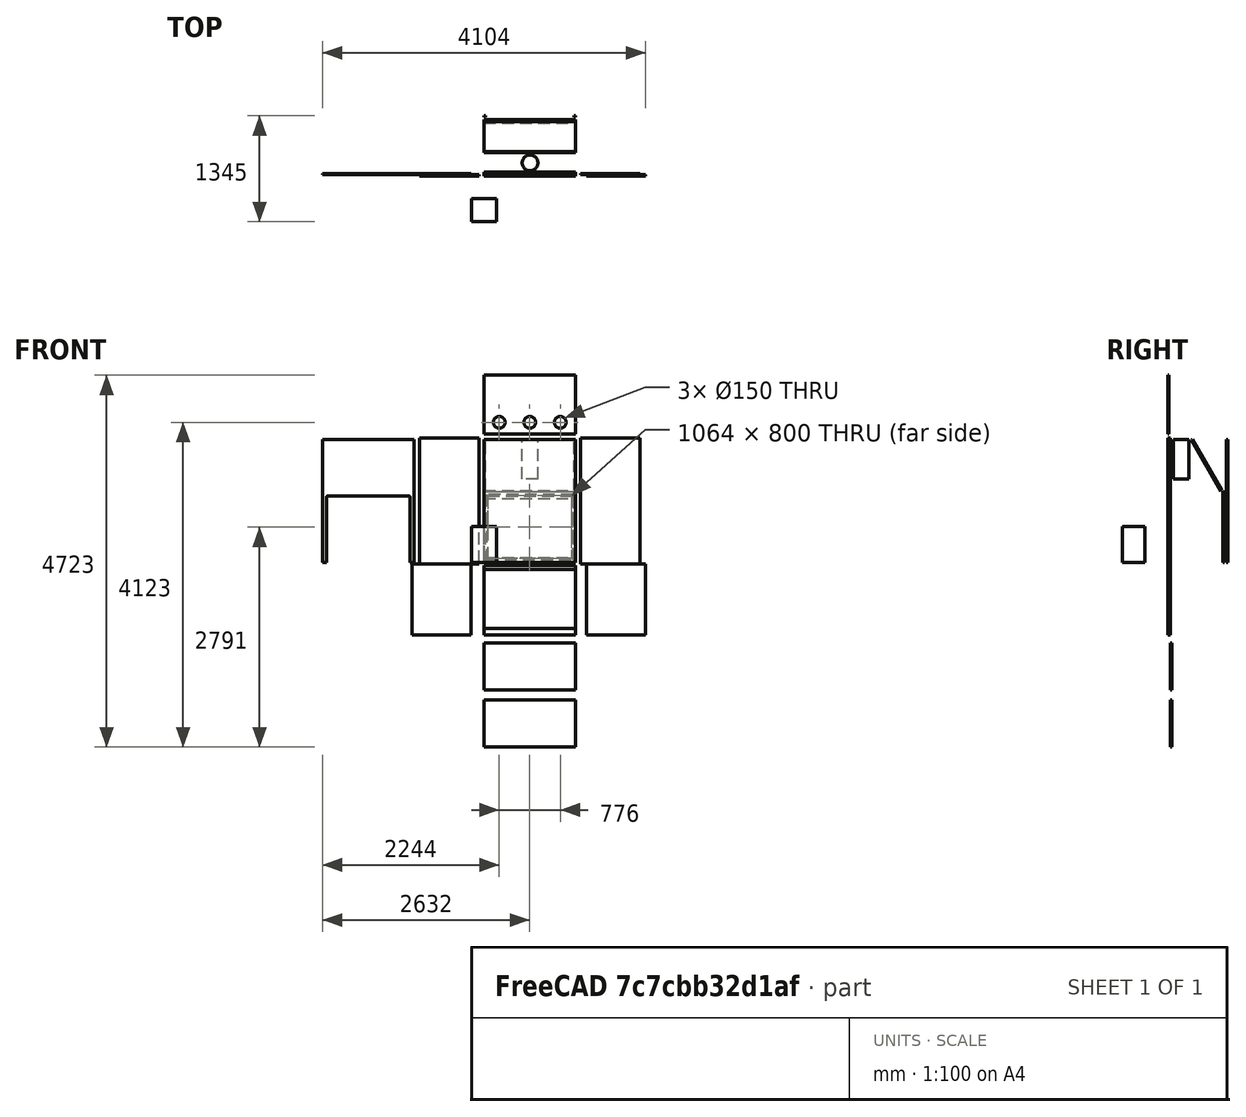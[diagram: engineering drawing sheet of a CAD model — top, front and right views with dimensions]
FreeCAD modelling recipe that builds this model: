
FCSTD DOCUMENT  (FreeCAD 0.18R4 (GitTag))
Label: fumehood1200_flat
License: All rights reserved
LicenseURL: http://en.wikipedia.org/wiki/All_rights_reserved
objects: TechDraw::DrawViewDimension×32, TechDraw::DrawProjGroup×14, Part::Box×13, TechDraw::DrawProjGroupItem×13, Sketcher::SketchObject×7, PartDesign::Body×5, PartDesign::Pad×4, App::Part×4, TechDraw::DrawSVGTemplate×3, TechDraw::DrawPage×3, PartDesign::Pocket×2, Spreadsheet::Sheet×1, Part::Cylinder×1
note: 38 computed .brp shape members not serialized (recipe doc carries the construction recipe); baked Part::Feature solids carry a one-line shape summary decoded from their .brp

FEATURE [Spreadsheet::Sheet] Spreadsheet  label="dim"
  cells = B2=Width; C2(dim_width)=1200; E2=FrontEdge; F2(dim_frontedge)=50; B3=Height; C3(dim_height)=1600; E3=FrontRadius; F3(dim_frontradius)=25; B4=Depth; C4(dim_depth)=750; E4=FrontOpening; F4(dim_frontopening)=850; B5=Thickness; C5(dim_thickness)=18; B6=Elevation; C6(dim_elevation)=900; B8=WindowWidth; C8(dim_windowwidth)==dim_width - dim_thickness * 2; B9=WindowHeight; C9(dim_windowheight)=900; B10=WindowEdge; C10(dim_windowedge)=50
FEATURE [Part::Box] Box  label="BackWall"
  AttacherType = Attacher::AttachEngine3D
  Height = 1564
  Length = 1164
  Placement = pos=(0,-18,18) rot=(0,0,1;0rad)
  Width = 18
  expr: Width = dim.dim_thickness
  expr: Height = dim.dim_height - 2 * dim.dim_thickness
  expr: Length = dim.dim_width - 2 * dim.dim_thickness
FEATURE [Part::Box] Box001  label="Side1"
  AttacherType = Attacher::AttachEngine3D
  Height = 1600
  Length = 750
  Placement = pos=(1230,0,0) rot=(0,0,1;0rad)
  Width = 18
  expr: Height = dim.dim_height
  expr: Width = dim.dim_thickness
  expr: Length = dim.dim_depth
FEATURE [Part::Box] Box002  label="Side2"
  AttacherType = Attacher::AttachEngine3D
  Height = 1600
  Length = 750
  Placement = pos=(-65,1.44e-14,0) rot=(0,0,1;3.14159rad)
  Width = 18
  expr: Height = dim.dim_height
  expr: Width = dim.dim_thickness
  expr: Length = dim.dim_depth
FEATURE [Part::Box] Box004  label="Bottom"
  AttacherType = Attacher::AttachEngine3D
  Height = 750
  Length = 1164
  Placement = pos=(0,4e-15,-70) rot=(1,0,0;3.14159rad)
  Width = 18
  expr: Height = dim.dim_depth
  expr: Width = dim.dim_thickness
  expr: Length = dim.dim_width - 2 * dim.dim_thickness
FEATURE [Sketcher::SketchObject] Sketch
  MapMode = 5
  Placement = pos=(0,0,0) rot=(1,0,0;1.5708rad)
  Support = -> [XZ_Plane]
  expr: Constraints[26] = dim.dim_frontedge
  expr: Constraints[16] = dim.dim_frontopening
  expr: Constraints[14] = dim.dim_frontradius
  expr: Constraints[6] = dim.dim_height - 2 * dim.dim_thickness
  expr: Constraints[5] = dim.dim_width - 2 * dim.dim_thickness
  sketch-geometry (10):
    g0: LineSegment StartX=1164 StartY=0 StartZ=0 EndX=1164 EndY=1564 EndZ=0
    g1: LineSegment StartX=1164 StartY=1564 StartZ=0 EndX=0 EndY=1564 EndZ=0
    g2: LineSegment StartX=0 StartY=1564 StartZ=0 EndX=0 EndY=0 EndZ=0
    g3: LineSegment StartX=75 StartY=850 StartZ=0 EndX=1089 EndY=850 EndZ=0
    g4: LineSegment StartX=1114 StartY=825 StartZ=0 EndX=1114 EndY=0 EndZ=0
    g5: LineSegment StartX=50 StartY=0 StartZ=0 EndX=50 EndY=825 EndZ=0
    g6: ArcOfCircle CenterX=75 CenterY=825 CenterZ=0 NormalX=0 NormalY=0 NormalZ=1 AngleXU=0 Radius=25 StartAngle=1.5708 EndAngle=3.14159
    g7: ArcOfCircle CenterX=1089 CenterY=825 CenterZ=0 NormalX=0 NormalY=0 NormalZ=1 AngleXU=0 Radius=25 StartAngle=-1.8e-15 EndAngle=1.5708
    g8: LineSegment StartX=1114 StartY=0 StartZ=0 EndX=1164 EndY=0 EndZ=0
    g9: LineSegment StartX=0 StartY=0 StartZ=0 EndX=50 EndY=0 EndZ=0
  constraints (27):
    c: Coincident(g0,g1)
    c: Coincident(g1,g2)
    c: Horizontal(g1)
    c: Vertical(g0)
    c: Vertical(g2)
    c: DistanceX(g1,g1) = 1164
    c: DistanceY(g0,g0) = 1564
    c: Horizontal(g3)
    c: Vertical(g4)
    c: Vertical(g5)
    c: Tangent(g5,g6) = 1.5708
    c: Tangent(g3,g6) = 1.5708
    c: Tangent(g3,g7) = 1.5708
    c: Tangent(g4,g7) = 1.5708
    c: Radius(g6) = 25
    c: Equal(g6,g7)
    c: DistanceY(g2,g3) = 850
    c: PointOnObject(g5,g-1)
    c: PointOnObject(g4,g-1)
    c: PointOnObject(g0,g-1)
    c: Coincident(g8,g4)
    c: Coincident(g8,g0)
    c: Coincident(g2,g-1)
    c: Coincident(g9,g2)
    c: Coincident(g9,g5)
    c: Equal(g9,g8)
    c: DistanceX(g9,g9) = 50
FEATURE [PartDesign::Pad] Pad
  Length = 18
  Length2 = 100
  Placement = pos=(0,0,0) rot=(1,0,0;1.5708rad)
  Profile = -> Sketch
  Reversed = true
  Type = 0
  expr: Length = dim.dim_thickness
FEATURE [PartDesign::Body] Body  label="Front"
  Group = -> [Sketch,Pad]
  Origin = -> Origin
  Placement = pos=(-2050,0,18) rot=(0,0,1;0rad)
  Tip = -> Pad
FEATURE [Sketcher::SketchObject] Sketch001
  MapMode = 5
  Placement = pos=(0,0,0) rot=(1,0,0;1.5708rad)
  Support = -> [XZ_Plane001]
  expr: Constraints[34] = dim.dim_windowedge
  expr: Constraints[18] = dim.dim_windowheight
  expr: Constraints[17] = dim.dim_windowwidth
  sketch-geometry (12):
    g0: LineSegment StartX=0 StartY=0 StartZ=0 EndX=-1064 EndY=0 EndZ=0
    g1: LineSegment StartX=-1064 StartY=0 StartZ=0 EndX=-1064 EndY=800 EndZ=0
    g2: LineSegment StartX=-1064 StartY=800 StartZ=0 EndX=0 EndY=800 EndZ=0
    g3: LineSegment StartX=0 StartY=800 StartZ=0 EndX=0 EndY=0 EndZ=0
    g4: LineSegment StartX=50 StartY=850 StartZ=0 EndX=-1114 EndY=850 EndZ=0
    g5: LineSegment StartX=-1114 StartY=850 StartZ=0 EndX=-1114 EndY=-50 EndZ=0
    g6: LineSegment StartX=-1114 StartY=-50 StartZ=0 EndX=50 EndY=-50 EndZ=0
    g7: LineSegment StartX=50 StartY=-50 StartZ=0 EndX=50 EndY=850 EndZ=0
    g8: LineSegment [constr] StartX=-1064 StartY=800 StartZ=0 EndX=-1114 EndY=800 EndZ=0
    g9: LineSegment [constr] StartX=-1064 StartY=800 StartZ=0 EndX=-1064 EndY=850 EndZ=0
    g10: LineSegment [constr] StartX=0 StartY=0 StartZ=0 EndX=50 EndY=0 EndZ=0
    g11: LineSegment [constr] StartX=0 StartY=0 StartZ=0 EndX=0 EndY=-50 EndZ=0
  constraints (35):
    c: Coincident(g0,g1)
    c: Coincident(g1,g2)
    c: Coincident(g2,g3)
    c: Coincident(g3,g0)
    c: Horizontal(g0)
    c: Horizontal(g2)
    c: Vertical(g1)
    c: Vertical(g3)
    c: Coincident(g0,g-1)
    c: Coincident(g4,g5)
    c: Coincident(g5,g6)
    c: Coincident(g6,g7)
    c: Coincident(g7,g4)
    c: Horizontal(g4)
    c: Horizontal(g6)
    c: Vertical(g5)
    c: Vertical(g7)
    c: DistanceX(g4,g4) = 1164
    c: DistanceY(g5,g5) = 900
    c: Coincident(g8,g1)
    c: PointOnObject(g8,g5)
    c: Horizontal(g8)
    c: Coincident(g9,g1)
    c: PointOnObject(g9,g4)
    c: Vertical(g9)
    c: Coincident(g10,g0)
    c: PointOnObject(g10,g7)
    c: Coincident(g11,g0)
    c: PointOnObject(g11,g6)
    c: Horizontal(g10)
    c: Vertical(g11)
    c: Equal(g10,g11)
    c: Equal(g11,g8)
    c: Equal(g8,g9)
    c: DistanceX(g8,g8) = 50
FEATURE [PartDesign::Pad] Pad001
  Length = 18
  Length2 = 100
  Placement = pos=(0,0,0) rot=(1,0,0;1.5708rad)
  Profile = -> Sketch001
  Type = 0
  expr: Length = dim.dim_thickness
FEATURE [Sketcher::SketchObject] Sketch010
  MapMode = 5
  Support = -> [XY_Plane010]
  sketch-geometry (7):
    g0: LineSegment StartX=-160 StartY=145 StartZ=0 EndX=160 EndY=145 EndZ=0
    g1: LineSegment StartX=160 StartY=145 StartZ=0 EndX=160 EndY=-145 EndZ=0
    g2: LineSegment StartX=160 StartY=-145 StartZ=0 EndX=-160 EndY=-145 EndZ=0
    g3: LineSegment StartX=-160 StartY=-145 StartZ=0 EndX=-160 EndY=145 EndZ=0
    g4: LineSegment [constr] StartX=-160 StartY=145 StartZ=0 EndX=0 EndY=0 EndZ=0
    g5: LineSegment [constr] StartX=0 StartY=0 StartZ=0 EndX=160 EndY=145 EndZ=0
    g6: LineSegment [constr] StartX=160 StartY=-145 StartZ=0 EndX=0 EndY=0 EndZ=0
  constraints (18):
    c: Coincident(g0,g1)
    c: Coincident(g1,g2)
    c: Coincident(g2,g3)
    c: Coincident(g3,g0)
    c: Horizontal(g0)
    c: Horizontal(g2)
    c: Vertical(g1)
    c: Vertical(g3)
    c: DistanceY(g3,g3) = 290
    c: DistanceX(g0,g0) = 320
    c: Coincident(g0,g4)
    c: Coincident(g4,g-1)
    c: Coincident(g4,g5)
    c: Coincident(g5,g0)
    c: Coincident(g1,g6)
    c: Coincident(g6,g-1)
    c: Equal(g6,g5)
    c: Equal(g5,g4)
FEATURE [PartDesign::Pad] Pad010
  Length = 460
  Length2 = 100
  Profile = -> Sketch010
  Type = 0
FEATURE [PartDesign::Body] Body008  label="Printer"
  Group = -> [Sketch010,Pad010]
  Origin = -> Origin010
  Placement = pos=(0,-450,20) rot=(0,0,1;0rad)
  Tip = -> Pad010
FEATURE [Sketcher::SketchObject] Sketch011
  MapMode = 5
  Placement = pos=(0,0,0) rot=(0.57735,0.57735,0.57735;2.0944rad)
  Support = -> [YZ_Plane011]
  sketch-geometry (17):
    g0: LineSegment StartX=337.533 StartY=73.563 StartZ=0 EndX=380.615 EndY=-384.066 EndZ=0
    g1: LineSegment StartX=380.615 StartY=-384.066 StartZ=0 EndX=395.57 EndY=-900 EndZ=0
    g2: LineSegment StartX=395.57 StartY=-900 StartZ=0 EndX=136.956 EndY=-900 EndZ=0
    g3: LineSegment StartX=337.533 StartY=73.563 StartZ=0 EndX=268.981 EndY=671.761 EndZ=0
    g4: LineSegment StartX=268.981 StartY=671.761 StartZ=0 EndX=434.918 EndY=671.761 EndZ=0
    g5: LineSegment StartX=434.918 StartY=671.761 StartZ=0 EndX=337.533 EndY=73.563 EndZ=0
    g6: Circle CenterX=341.02 CenterY=900 CenterZ=0 NormalX=0 NormalY=0 NormalZ=1 AngleXU=0 Radius=148.256
    g7: LineSegment StartX=268.981 StartY=671.761 StartZ=0 EndX=257.081 EndY=260 EndZ=0
    g8: LineSegment StartX=257.081 StartY=260 StartZ=0 EndX=434.918 EndY=671.761 EndZ=0
    g9: LineSegment StartX=257.081 StartY=260 StartZ=0 EndX=-129.183 EndY=320.639 EndZ=0
    g10: LineSegment StartX=-129.183 StartY=320.639 StartZ=0 EndX=-129.183 EndY=239.552 EndZ=0
    g11: LineSegment StartX=-129.183 StartY=239.552 StartZ=0 EndX=257.081 EndY=260 EndZ=0
    g12: LineSegment StartX=337.533 StartY=73.563 StartZ=0 EndX=292.125 EndY=-384.066 EndZ=0
    g13: LineSegment StartX=292.125 StartY=-384.066 StartZ=0 EndX=395.57 EndY=-900 EndZ=0
    g14: LineSegment StartX=292.125 StartY=-384.066 StartZ=0 EndX=380.615 EndY=-384.066 EndZ=0
    g15: LineSegment StartX=-129.183 StartY=320.639 StartZ=0 EndX=-200.089 EndY=304.859 EndZ=0
    g16: LineSegment StartX=-129.183 StartY=239.552 StartZ=0 EndX=-200.089 EndY=304.859 EndZ=0
  constraints (28):
    c: Coincident(g1,g0)
    c: Coincident(g2,g1)
    c: Horizontal(g2)
    c: DistanceY(g2,g-1) = 900
    c: Coincident(g3,g0)
    c: Coincident(g4,g3)
    c: Horizontal(g4)
    c: Coincident(g5,g4)
    c: Coincident(g5,g0)
    c: DistanceY(g2,g6) = 1800
    c: Coincident(g7,g3)
    c: Coincident(g8,g7)
    c: Coincident(g8,g4)
    c: Coincident(g7,g9)
    c: Coincident(g9,g10)
    c: Vertical(g10)
    c: Coincident(g10,g11)
    c: Coincident(g11,g9)
    c: Coincident(g0,g12)
    c: Coincident(g12,g13)
    c: Coincident(g13,g1)
    c: Coincident(g14,g12)
    c: Coincident(g14,g0)
    c: Horizontal(g14)
    c: DistanceY(g1,g7) = 1160
    c: Coincident(g15,g9)
    c: Coincident(g16,g10)
    c: Coincident(g16,g15)
FEATURE [PartDesign::Body] Body009  label="human"
  Group = -> [Sketch011]
  Origin = -> Origin011
  Placement = pos=(0,-140,0) rot=(0,0,1;0rad)
FEATURE [App::Part] Part  label="Human"
  Group = -> [Body008,Body009]
  Origin = -> Origin002
  Placement = pos=(400,800,0) rot=(0,0,1;0rad)
FEATURE [Part::Box] Box005  label="Rail1"
  AttacherType = Attacher::AttachEngine3D
  Height = 1564
  Length = 20
  Placement = pos=(1144,730,18) rot=(0,0,1;0rad)
  Width = 20
  expr: Height = dim.dim_height - dim.dim_thickness * 2
FEATURE [Part::Box] Box006  label="Rail2"
  AttacherType = Attacher::AttachEngine3D
  Height = 1564
  Length = 20
  Placement = pos=(0,730,18) rot=(0,0,1;0rad)
  Width = 20
  expr: Height = dim.dim_height - dim.dim_thickness * 2
FEATURE [Sketcher::SketchObject] Sketch012
  ExternalGeometry = -> [Pad001]
  MapMode = 5
  Placement = pos=(0,0,0) rot=(-1,0,0;1.5708rad)
  Support = -> [Pad001]
  sketch-geometry (8):
    g0: LineSegment StartX=-1079 StartY=15 StartZ=0 EndX=15 EndY=15 EndZ=0
    g1: LineSegment StartX=15 StartY=15 StartZ=0 EndX=15 EndY=-815 EndZ=0
    g2: LineSegment StartX=15 StartY=-815 StartZ=0 EndX=-1079 EndY=-815 EndZ=0
    g3: LineSegment StartX=-1079 StartY=-815 StartZ=0 EndX=-1079 EndY=15 EndZ=0
    g4: LineSegment [constr] StartX=-1064 StartY=0 StartZ=0 EndX=-1079 EndY=0 EndZ=0
    g5: LineSegment [constr] StartX=-1064 StartY=0 StartZ=0 EndX=-1064 EndY=15 EndZ=0
    g6: LineSegment [constr] StartX=0 StartY=-800 StartZ=0 EndX=15 EndY=-800 EndZ=0
    g7: LineSegment [constr] StartX=0 StartY=-800 StartZ=0 EndX=0 EndY=-815 EndZ=0
  constraints (24):
    c: Coincident(g0,g1)
    c: Coincident(g1,g2)
    c: Coincident(g2,g3)
    c: Coincident(g3,g0)
    c: Horizontal(g0)
    c: Horizontal(g2)
    c: Vertical(g1)
    c: Vertical(g3)
    c: Coincident(g4,g-3)
    c: PointOnObject(g4,g3)
    c: Horizontal(g4)
    c: Coincident(g5,g4)
    c: PointOnObject(g5,g0)
    c: Vertical(g5)
    c: Coincident(g6,g-4)
    c: PointOnObject(g6,g1)
    c: Horizontal(g6)
    c: Coincident(g7,g6)
    c: PointOnObject(g7,g2)
    c: Vertical(g7)
    c: Equal(g6,g7)
    c: Equal(g7,g4)
    c: Equal(g4,g5)
    c: DistanceX(g4,g4) = 15
FEATURE [PartDesign::Pocket] Pocket
  BaseFeature = -> Pad001
  Length = 6
  Length2 = 100
  Placement = pos=(0,0,0) rot=(1,0,0;1.5708rad)
  Profile = -> Sketch012
  Type = 0
FEATURE [PartDesign::Body] Body001  label="Window"
  Group = -> [Sketch001,Pad001,Sketch012,Pocket]
  Origin = -> Origin001
  Placement = pos=(1114,700,68) rot=(0,0,1;0rad)
  Tip = -> Pocket
  expr: Placement.Base.x = dim.dim_width - 2 * dim.dim_thickness - 50
FEATURE [App::Part] Part001  label="Window001"
  Group = -> [Body001]
  Origin = -> Origin012
  Placement = pos=(0,0,350) rot=(0,0,1;0rad)
FEATURE [Part::Box] Box007  label="ShelfSide1"
  AttacherType = Attacher::AttachEngine3D
  Height = 900
  Length = 18
  Placement = pos=(-166,-3.29e-14,-900) rot=(0,0,1;1.5708rad)
  Width = 750
  expr: Length = dim.dim_thickness
  expr: Width = dim.dim_depth
  expr: Height = dim.dim_elevation
FEATURE [Part::Box] Box008  label="ShelfSide2"
  AttacherType = Attacher::AttachEngine3D
  Height = 900
  Length = 18
  Placement = pos=(1304,-3.11e-14,-900) rot=(0,0,1;4.71239rad)
  Width = 750
  expr: Height = dim.dim_elevation
  expr: Width = dim.dim_depth
  expr: Length = dim.dim_thickness
FEATURE [Part::Box] Box009  label="ShelfTop"
  AttacherType = Attacher::AttachEngine3D
  Height = 750
  Length = 1164
  Placement = pos=(0,-1.89e-14,85) rot=(0,0,1;0rad)
  Width = 18
  expr: Height = dim.dim_depth
  expr: Width = dim.dim_thickness
  expr: Length = dim.dim_width - 2 * dim.dim_thickness
FEATURE [Part::Box] Box010  label="ShelfBack"
  AttacherType = Attacher::AttachEngine3D
  Height = 882
  Length = 1164
  Placement = pos=(0,0,-900) rot=(0,0,1;0rad)
  Width = 18
  expr: Width = dim.dim_thickness
  expr: Height = dim.dim_elevation - dim.dim_thickness
  expr: Length = dim.dim_width - 2 * dim.dim_thickness
FEATURE [Part::Box] Box011  label="ShelfMid1"
  AttacherType = Attacher::AttachEngine3D
  Height = 18
  Length = 1164
  Placement = pos=(0,18,-1000) rot=(1,0,0;4.71239rad)
  Width = 600
  expr: Length = dim.dim_width - 2 * dim.dim_thickness
  expr: Width = dim.dim_depth - 150
  expr: Height = dim.dim_thickness
FEATURE [Part::Box] Box012  label="ShelfMid2"
  AttacherType = Attacher::AttachEngine3D
  Height = 18
  Length = 1164
  Placement = pos=(0,18,-1723) rot=(1,0,0;4.71239rad)
  Width = 600
  expr: Height = dim.dim_thickness
  expr: Width = dim.dim_depth - 150
  expr: Length = dim.dim_width - 2 * dim.dim_thickness
FEATURE [App::Part] Part002  label="Shelf"
  Group = -> [Box007,Box008,Box009,Box010,Box011,Box012]
  Origin = -> Origin013
  Placement = pos=(0,0,-1000) rot=(0,0,1;0rad)
FEATURE [Part::Cylinder] Cylinder
  Angle = 360
  AttacherType = Attacher::AttachEngine3D
  Height = 500
  Placement = pos=(586,152,1082) rot=(0,0,1;0rad)
  Radius = 100
FEATURE [Part::Box] Box013  label="Airway"
  AttacherType = Attacher::AttachEngine3D
  Height = 750
  Length = 1164
  Placement = pos=(0,298,1582) rot=(1,0,0;3.66519rad)
  Width = 18
  expr: Width = dim.dim_thickness
  expr: Length = dim.dim_width - 2 * dim.dim_thickness
FEATURE [Sketcher::SketchObject] Sketch013
  MapMode = 5
  Support = -> [XY_Plane014]
  expr: Constraints[10] = dim.dim_width - 2 * dim.dim_thickness
  expr: Constraints[9] = dim.dim_depth
  sketch-geometry (4):
    g0: LineSegment StartX=0 StartY=0 StartZ=0 EndX=1164 EndY=0 EndZ=0
    g1: LineSegment StartX=1164 StartY=0 StartZ=0 EndX=1164 EndY=750 EndZ=0
    g2: LineSegment StartX=1164 StartY=750 StartZ=0 EndX=0 EndY=750 EndZ=0
    g3: LineSegment StartX=0 StartY=750 StartZ=0 EndX=0 EndY=0 EndZ=0
  constraints (11):
    c: Coincident(g0,g1)
    c: Coincident(g1,g2)
    c: Coincident(g2,g3)
    c: Coincident(g3,g0)
    c: Horizontal(g0)
    c: Horizontal(g2)
    c: Vertical(g1)
    c: Vertical(g3)
    c: Coincident(g0,g-1)
    c: DistanceY(g1,g1) = 750
    c: DistanceX(g2,g2) = 1164
FEATURE [PartDesign::Pad] Pad011
  Length = 18
  Length2 = 100
  Profile = -> Sketch013
  Type = 0
  expr: Length = dim.dim_thickness
FEATURE [Sketcher::SketchObject] Sketch014
  ExternalGeometry = -> [Pad011]
  MapMode = 5
  Placement = pos=(0,0,18) rot=(0,0,1;0rad)
  Support = -> [Pad011]
  sketch-geometry (11):
    g0: LineSegment [constr] StartX=0 StartY=0 StartZ=0 EndX=194 EndY=150 EndZ=0
    g1: LineSegment [constr] StartX=194 StartY=150 StartZ=0 EndX=388 EndY=0 EndZ=0
    g2: LineSegment [constr] StartX=388 StartY=0 StartZ=0 EndX=582 EndY=150 EndZ=0
    g3: LineSegment [constr] StartX=582 StartY=150 StartZ=0 EndX=776 EndY=0 EndZ=0
    g4: LineSegment [constr] StartX=776 StartY=0 StartZ=0 EndX=970 EndY=150 EndZ=0
    g5: LineSegment [constr] StartX=970 StartY=150 StartZ=0 EndX=1164 EndY=0 EndZ=0
    g6: LineSegment [constr] StartX=194 StartY=150 StartZ=0 EndX=582 EndY=150 EndZ=0
    g7: LineSegment [constr] StartX=582 StartY=150 StartZ=0 EndX=970 EndY=150 EndZ=0
    g8: Circle CenterX=582 CenterY=150 CenterZ=0 NormalX=0 NormalY=0 NormalZ=1 AngleXU=0 Radius=75
    g9: Circle CenterX=970 CenterY=150 CenterZ=0 NormalX=0 NormalY=0 NormalZ=1 AngleXU=0 Radius=75
    g10: Circle CenterX=194 CenterY=150 CenterZ=0 NormalX=0 NormalY=0 NormalZ=1 AngleXU=0 Radius=75
  constraints (27):
    c: Coincident(g-1,g0)
    c: Coincident(g0,g1)
    c: PointOnObject(g1,g-3)
    c: Coincident(g1,g2)
    c: Coincident(g2,g3)
    c: PointOnObject(g3,g-3)
    c: Coincident(g3,g4)
    c: Coincident(g4,g5)
    c: Coincident(g5,g-3)
    c: Coincident(g0,g6)
    c: Coincident(g6,g2)
    c: Horizontal(g6)
    c: Coincident(g6,g7)
    c: Coincident(g7,g4)
    c: Horizontal(g7)
    c: Equal(g1,g0)
    c: Equal(g0,g2)
    c: Equal(g2,g3)
    c: Equal(g3,g4)
    c: Equal(g4,g5)
    c: Coincident(g8,g2)
    c: Coincident(g9,g4)
    c: Coincident(g10,g0)
    c: Diameter(g10) = 150
    c: Equal(g10,g8)
    c: Equal(g10,g9)
    c: DistanceY(g-1,g10) = 150
FEATURE [PartDesign::Pocket] Pocket001
  BaseFeature = -> Pad011
  Length = 5
  Length2 = 100
  Profile = -> Sketch014
  Type = 1
FEATURE [PartDesign::Body] Body010  label="Top001"
  Group = -> [Sketch013,Pad011,Sketch014,Pocket001]
  Origin = -> Origin014
  Placement = pos=(0,0,1650) rot=(1,0,0;1.5708rad)
  Tip = -> Pocket001
FEATURE [TechDraw::DrawSVGTemplate] Template
  EditableTexts = Designed_by_Name=Intech Studio; Drawing_number=Drawing number; FC-Date=2020.10.09.; FC-SC=0.04; FC-SH=Sheet; FC-Title=120cm szekrény; Subtitle=18mm bútorlap; Weight=Weight
  Height = 210
  Orientation = 1
  Width = 297
FEATURE [TechDraw::DrawSVGTemplate] Template001
  EditableTexts = Designed_by_Name=Intech Studio; Drawing_number=Drawing number; FC-Date=2020.10.09.; FC-SC=0.04; FC-SH=Sheet; FC-Title=120cm polc; Subtitle=18mm bútorlap; Weight=Weight
  Height = 210
  Orientation = 1
  Width = 297
FEATURE [TechDraw::DrawProjGroup] ProjGroup
  AutoDistribute = true
  LockPosition = false
  ProjectionType = 0
  Rotation = 0
  Scale = 0.04
  ScaleType = 0
  Source = -> [Box]
  X = 141.606
  Y = 130.278
  spacingX = 15
  spacingY = 15
FEATURE [TechDraw::DrawProjGroupItem] ProjItem  label="Front001"
  CoarseView = false
  Direction = (0,1,0)
  Focus = 100
  HardHidden = false
  IsoCount = 0
  IsoHidden = false
  IsoVisible = false
  LockPosition = true
  Perspective = false
  Rotation = 0
  RotationVector = (-1,0,0)
  Scale = 0.04
  ScaleType = 2
  SeamHidden = false
  SeamVisible = false
  SmoothHidden = false
  SmoothVisible = false
  Source = -> [Box]
  Type = 0
  X = 0
  Y = 0
FEATURE [TechDraw::DrawProjGroup] ProjGroup001
  Anchor = -> ProjItem
  AutoDistribute = true
  LockPosition = false
  ProjectionType = 0
  Rotation = 0
  Scale = 0.04
  ScaleType = 0
  Source = -> [Box]
  Views = -> [ProjItem]
  X = 103.196
  Y = 111.237
  spacingX = 15
  spacingY = 15
FEATURE [TechDraw::DrawProjGroupItem] ProjItem001  label="Front002"
  CoarseView = false
  Direction = (0,1,0)
  Focus = 100
  HardHidden = false
  IsoCount = 0
  IsoHidden = false
  IsoVisible = false
  LockPosition = true
  Perspective = false
  Rotation = 0
  RotationVector = (-1,0,0)
  Scale = 0.04
  ScaleType = 2
  SeamHidden = false
  SeamVisible = false
  SmoothHidden = false
  SmoothVisible = false
  Source = -> [Box001]
  Type = 0
  X = 0
  Y = 0
FEATURE [TechDraw::DrawProjGroup] ProjGroup002
  Anchor = -> ProjItem001
  AutoDistribute = true
  LockPosition = false
  ProjectionType = 0
  Rotation = 0
  Scale = 0.04
  ScaleType = 0
  Source = -> [Box001]
  Views = -> [ProjItem001]
  X = 44.1046
  Y = 110.909
  spacingX = 15
  spacingY = 15
FEATURE [TechDraw::DrawProjGroupItem] ProjItem002  label="Front003"
  CoarseView = false
  Direction = (0,1,0)
  Focus = 100
  HardHidden = false
  IsoCount = 0
  IsoHidden = false
  IsoVisible = false
  LockPosition = true
  Perspective = false
  Rotation = 0
  RotationVector = (-1,0,0)
  Scale = 0.04
  ScaleType = 2
  SeamHidden = false
  SeamVisible = false
  SmoothHidden = false
  SmoothVisible = false
  Source = -> [Box002]
  Type = 0
  X = 0
  Y = 0
FEATURE [TechDraw::DrawProjGroup] ProjGroup003
  Anchor = -> ProjItem002
  AutoDistribute = true
  LockPosition = false
  ProjectionType = 0
  Rotation = 0
  Scale = 0.04
  ScaleType = 0
  Source = -> [Box002]
  Views = -> [ProjItem002]
  X = 162.945
  Y = 111.894
  spacingX = 15
  spacingY = 15
FEATURE [TechDraw::DrawProjGroupItem] ProjItem003  label="Front004"
  CoarseView = false
  Direction = (0,1,0)
  Focus = 100
  HardHidden = false
  IsoCount = 0
  IsoHidden = false
  IsoVisible = false
  LockPosition = true
  Perspective = false
  Rotation = 0
  RotationVector = (-1,0,0)
  Scale = 0.04
  ScaleType = 2
  SeamHidden = false
  SeamVisible = false
  SmoothHidden = false
  SmoothVisible = false
  Source = -> [Box004]
  Type = 0
  X = 0
  Y = 0
FEATURE [TechDraw::DrawProjGroup] ProjGroup004
  Anchor = -> ProjItem003
  AutoDistribute = true
  LockPosition = false
  ProjectionType = 0
  Rotation = 0
  Scale = 0.04
  ScaleType = 0
  Source = -> [Box004]
  Views = -> [ProjItem003]
  X = 103.853
  Y = 42.2971
  spacingX = 15
  spacingY = 15
FEATURE [TechDraw::DrawProjGroupItem] ProjItem004  label="Front005"
  CoarseView = false
  Direction = (0,1,0)
  Focus = 100
  HardHidden = false
  IsoCount = 0
  IsoHidden = false
  IsoVisible = false
  LockPosition = true
  Perspective = false
  Rotation = 0
  RotationVector = (-1,0,0)
  Scale = 0.04
  ScaleType = 2
  SeamHidden = false
  SeamVisible = false
  SmoothHidden = false
  SmoothVisible = false
  Source = -> [Body010]
  Type = 0
  X = 0
  Y = 0
FEATURE [TechDraw::DrawProjGroup] ProjGroup005
  Anchor = -> ProjItem004
  AutoDistribute = true
  LockPosition = false
  ProjectionType = 0
  Rotation = 0
  Scale = 0.04
  ScaleType = 0
  Source = -> [Body010]
  Views = -> [ProjItem004]
  X = 102.157
  Y = 169.29
  spacingX = 15
  spacingY = 15
FEATURE [TechDraw::DrawProjGroupItem] ProjItem005  label="Front006"
  CoarseView = false
  Direction = (0,1,0)
  Focus = 100
  HardHidden = false
  IsoCount = 0
  IsoHidden = false
  IsoVisible = false
  LockPosition = true
  Perspective = false
  Rotation = 0
  RotationVector = (-1,0,0)
  Scale = 0.04
  ScaleType = 2
  SeamHidden = false
  SeamVisible = false
  SmoothHidden = false
  SmoothVisible = false
  Source = -> [Body]
  Type = 0
  X = 0
  Y = 0
FEATURE [TechDraw::DrawProjGroup] ProjGroup006
  Anchor = -> ProjItem005
  AutoDistribute = true
  LockPosition = false
  ProjectionType = 0
  Rotation = 0
  Scale = 0.04
  ScaleType = 0
  Source = -> [Body]
  Views = -> [ProjItem005]
  X = 221.051
  Y = 110.909
  spacingX = 15
  spacingY = 15
FEATURE [TechDraw::DrawViewDimension] Dimension
  Arbitrary = false
  FormatSpec = %.2f
  LockPosition = false
  MeasureType = 1
  OverTolerance = 0
  References2D = -> [ProjItem001]
  Rotation = 0
  Scale = 0.04
  ScaleType = 0
  Type = 1
  UnderTolerance = 0
  X = 0.547145
  Y = 41.575
FEATURE [TechDraw::DrawViewDimension] Dimension001
  Arbitrary = false
  FormatSpec = %.2f
  LockPosition = false
  MeasureType = 1
  OverTolerance = 0
  References2D = -> [ProjItem001]
  Rotation = 0
  Scale = 0.04
  ScaleType = 0
  Type = 2
  UnderTolerance = 0
  X = -24.8486
  Y = 1.64144
FEATURE [TechDraw::DrawViewDimension] Dimension002
  Arbitrary = false
  FormatSpec = %.2f
  LockPosition = false
  MeasureType = 1
  OverTolerance = 0
  References2D = -> [ProjItem]
  Rotation = 0
  Scale = 0.04
  ScaleType = 0
  Type = 1
  UnderTolerance = 0
  X = 0.547145
  Y = 38.94
FEATURE [TechDraw::DrawViewDimension] Dimension003
  Arbitrary = false
  FormatSpec = %.2f
  LockPosition = false
  MeasureType = 1
  OverTolerance = 0
  References2D = -> [ProjItem]
  Rotation = 0
  Scale = 0.04
  ScaleType = 0
  Type = 2
  UnderTolerance = 0
  X = -33.6758
  Y = -0.273573
FEATURE [TechDraw::DrawViewDimension] Dimension004
  Arbitrary = false
  FormatSpec = %.2f
  LockPosition = false
  MeasureType = 1
  OverTolerance = 0
  References2D = -> [ProjItem004]
  Rotation = 0
  Scale = 0.04
  ScaleType = 0
  Type = 2
  UnderTolerance = 0
  X = -35.0436
  Y = -1.09429
FEATURE [TechDraw::DrawViewDimension] Dimension006
  Arbitrary = false
  FormatSpec = %.2f
  LockPosition = false
  MeasureType = 1
  OverTolerance = 0
  References2D = -> [ProjItem003]
  Rotation = 0
  Scale = 0.04
  ScaleType = 0
  Type = 1
  UnderTolerance = 0
  X = 0.820718
  Y = 24.3015
FEATURE [TechDraw::DrawViewDimension] Dimension007
  Arbitrary = false
  FormatSpec = %.2f
  LockPosition = false
  MeasureType = 1
  OverTolerance = 0
  References2D = -> [ProjItem003]
  Rotation = 0
  Scale = 0.04
  ScaleType = 0
  Type = 2
  UnderTolerance = 0
  X = -34.2229
  Y = -0.273573
FEATURE [TechDraw::DrawViewDimension] Dimension008
  Arbitrary = false
  FormatSpec = %.2f
  LockPosition = false
  MeasureType = 1
  OverTolerance = 0
  References2D = -> [ProjItem002]
  Rotation = 0
  Scale = 0.04
  ScaleType = 0
  Type = 2
  UnderTolerance = 0
  X = -24.0279
  Y = -0.547145
FEATURE [TechDraw::DrawViewDimension] Dimension009
  Arbitrary = false
  FormatSpec = %.2f
  LockPosition = false
  MeasureType = 1
  OverTolerance = 0
  References2D = -> [ProjItem002]
  Rotation = 0
  Scale = 0.04
  ScaleType = 0
  Type = 1
  UnderTolerance = 0
  X = 0.820718
  Y = 41.0279
FEATURE [TechDraw::DrawViewDimension] Dimension010
  Arbitrary = false
  FormatSpec = %.2f
  LockPosition = false
  MeasureType = 1
  OverTolerance = 0
  References2D = -> [ProjItem005]
  Rotation = 0
  Scale = 0.04
  ScaleType = 0
  Type = 2
  UnderTolerance = 0
  X = -36.913
  Y = -2.64834
FEATURE [TechDraw::DrawViewDimension] Dimension011
  Arbitrary = false
  FormatSpec = %.2f
  LockPosition = false
  MeasureType = 1
  OverTolerance = 0
  References2D = -> [ProjItem005]
  Rotation = 0
  Scale = 0.04
  ScaleType = 0
  Type = 1
  UnderTolerance = 0
  X = 0.547145
  Y = 40.3079
FEATURE [TechDraw::DrawViewDimension] Dimension012
  Arbitrary = false
  FormatSpec = %.2f
  LockPosition = false
  MeasureType = 1
  OverTolerance = 0
  References2D = -> [ProjItem005]
  Rotation = 0
  Scale = 0.04
  ScaleType = 0
  Type = 1
  UnderTolerance = 0
  X = 0.63327
  Y = -33.4964
FEATURE [TechDraw::DrawViewDimension] Dimension013
  Arbitrary = false
  FormatSpec = %.2f
  LockPosition = false
  MeasureType = 1
  OverTolerance = 0
  References2D = -> [ProjItem005]
  Rotation = 0
  Scale = 0.04
  ScaleType = 0
  Type = 2
  UnderTolerance = 0
  X = 31.3162
  Y = -12.2644
FEATURE [TechDraw::DrawViewDimension] Dimension014
  Arbitrary = false
  FormatSpec = %.2f
  LockPosition = false
  MeasureType = 1
  OverTolerance = 0
  References2D = -> [ProjItem004]
  Rotation = 0
  Scale = 0.04
  ScaleType = 0
  Type = 1
  UnderTolerance = 0
  X = 0.273573
  Y = 23.7543
FEATURE [TechDraw::DrawViewDimension] Dimension015
  Arbitrary = false
  FormatSpec = ⌀%.2f
  LockPosition = false
  MeasureType = 1
  OverTolerance = 0
  References2D = -> [ProjItem004]
  Rotation = 0
  Scale = 0.04
  ScaleType = 0
  Type = 5
  UnderTolerance = 0
  X = 43.2207
  Y = 0.633271
FEATURE [TechDraw::DrawViewDimension] Dimension016
  Arbitrary = false
  FormatSpec = %.2f
  LockPosition = false
  MeasureType = 1
  OverTolerance = 0
  References2D = -> [ProjItem004]
  Rotation = 0
  Scale = 0.04
  ScaleType = 0
  Type = 2
  UnderTolerance = 0
  X = 30.0073
  Y = -26.4069
FEATURE [TechDraw::DrawViewDimension] Dimension017
  Arbitrary = false
  FormatSpec = %.2f
  LockPosition = false
  MeasureType = 1
  OverTolerance = 0
  References2D = -> [ProjItem004]
  Rotation = 0
  Scale = 0.04
  ScaleType = 0
  Type = 1
  UnderTolerance = 0
  X = 0.474953
  Y = 3.19045
FEATURE [TechDraw::DrawPage] Page  label="Box"
  KeepUpdated = true
  ProjectionType = 0
  Scale = 0.04
  Template = -> Template
  Views = -> [ProjGroup,ProjGroup001,ProjGroup002,ProjGroup003,ProjGroup004,ProjGroup005,ProjGroup006,Dimension,Dimension001,Dimension002,Dimension003,Dimension004,Dimension006,Dimension007,Dimension008,Dimension009,Dimension010,Dimension011,Dimension012,Dimension013,Dimension014,Dimension015,Dimension016,Dimension017]
FEATURE [App::Part] Part003  label="Box001"
  Group = -> [Box006,Box005,Part001,Part,Body,Box004,Box002,Box001,Box,Body010,Box013,Cylinder]
  Origin = -> Origin015
FEATURE [TechDraw::DrawProjGroupItem] ProjItem006  label="Front007"
  CoarseView = false
  Direction = (0,1,0)
  Focus = 100
  HardHidden = false
  IsoCount = 0
  IsoHidden = false
  IsoVisible = false
  LockPosition = true
  Perspective = false
  Rotation = 0
  RotationVector = (1,0,0)
  Scale = 0.04
  ScaleType = 2
  SeamHidden = false
  SeamVisible = false
  SmoothHidden = false
  SmoothVisible = false
  Source = -> [Box010]
  Type = 0
  X = 0
  Y = 0
FEATURE [TechDraw::DrawProjGroup] ProjGroup007
  Anchor = -> ProjItem006
  AutoDistribute = true
  LockPosition = false
  ProjectionType = 0
  Rotation = 0
  Scale = 0.04
  ScaleType = 0
  Source = -> [Box010]
  Views = -> [ProjItem006]
  X = 105.166
  Y = 126.01
  spacingX = 15
  spacingY = 15
FEATURE [TechDraw::DrawProjGroupItem] ProjItem007  label="Front008"
  CoarseView = false
  Direction = (0,1,0)
  Focus = 100
  HardHidden = false
  IsoCount = 0
  IsoHidden = false
  IsoVisible = false
  LockPosition = true
  Perspective = false
  Rotation = 0
  RotationVector = (-1,0,0)
  Scale = 0.04
  ScaleType = 2
  SeamHidden = false
  SeamVisible = false
  SmoothHidden = false
  SmoothVisible = false
  Source = -> [Box007]
  Type = 0
  X = 0
  Y = 0
FEATURE [TechDraw::DrawProjGroup] ProjGroup008
  Anchor = -> ProjItem007
  AutoDistribute = true
  LockPosition = false
  ProjectionType = 0
  Rotation = 0
  Scale = 0.04
  ScaleType = 0
  Source = -> [Box007]
  Views = -> [ProjItem007]
  X = 49.8314
  Y = 125.226
  spacingX = 15
  spacingY = 15
FEATURE [TechDraw::DrawProjGroupItem] ProjItem008  label="Front009"
  CoarseView = false
  Direction = (0,1,0)
  Focus = 100
  HardHidden = false
  IsoCount = 0
  IsoHidden = false
  IsoVisible = false
  LockPosition = true
  Perspective = false
  Rotation = 0
  RotationVector = (-1,0,0)
  Scale = 0.04
  ScaleType = 2
  SeamHidden = false
  SeamVisible = false
  SmoothHidden = false
  SmoothVisible = false
  Source = -> [Box008]
  Type = 0
  X = 0
  Y = 0
FEATURE [TechDraw::DrawProjGroup] ProjGroup009
  Anchor = -> ProjItem008
  AutoDistribute = true
  LockPosition = false
  ProjectionType = 0
  Rotation = 0
  Scale = 0.04
  ScaleType = 0
  Source = -> [Box008]
  Views = -> [ProjItem008]
  X = 160.318
  Y = 125.682
  spacingX = 15
  spacingY = 15
FEATURE [TechDraw::DrawProjGroupItem] ProjItem009  label="Front010"
  CoarseView = false
  Direction = (0,1,0)
  Focus = 100
  HardHidden = false
  IsoCount = 0
  IsoHidden = false
  IsoVisible = false
  LockPosition = true
  Perspective = false
  Rotation = 0
  RotationVector = (-1,0,0)
  Scale = 0.04
  ScaleType = 2
  SeamHidden = false
  SeamVisible = false
  SmoothHidden = false
  SmoothVisible = false
  Source = -> [Box009]
  Type = 0
  X = 0
  Y = 0
FEATURE [TechDraw::DrawProjGroup] ProjGroup010
  Anchor = -> ProjItem009
  AutoDistribute = true
  LockPosition = false
  ProjectionType = 0
  Rotation = 0
  Scale = 0.04
  ScaleType = 0
  Source = -> [Box009]
  Views = -> [ProjItem009]
  X = 104.838
  Y = 172.189
  spacingX = 15
  spacingY = 15
FEATURE [TechDraw::DrawProjGroupItem] ProjItem010  label="Front011"
  CoarseView = false
  Direction = (0,1,0)
  Focus = 100
  HardHidden = false
  IsoCount = 0
  IsoHidden = false
  IsoVisible = false
  LockPosition = true
  Perspective = false
  Rotation = 0
  RotationVector = (-1,0,0)
  Scale = 0.04
  ScaleType = 2
  SeamHidden = false
  SeamVisible = false
  SmoothHidden = false
  SmoothVisible = false
  Source = -> [Box011]
  Type = 0
  X = 0
  Y = 0
FEATURE [TechDraw::DrawProjGroup] ProjGroup011
  Anchor = -> ProjItem010
  AutoDistribute = true
  LockPosition = false
  ProjectionType = 0
  Rotation = 0
  Scale = 0.04
  ScaleType = 0
  Source = -> [Box011]
  Views = -> [ProjItem010]
  X = 105.494
  Y = 76.7673
  spacingX = 15
  spacingY = 15
FEATURE [TechDraw::DrawProjGroupItem] ProjItem011  label="Front012"
  CoarseView = false
  Direction = (0,1,0)
  Focus = 100
  HardHidden = false
  IsoCount = 0
  IsoHidden = false
  IsoVisible = false
  LockPosition = true
  Perspective = false
  Rotation = 0
  RotationVector = (-1,0,0)
  Scale = 0.04
  ScaleType = 2
  SeamHidden = false
  SeamVisible = false
  SmoothHidden = false
  SmoothVisible = false
  Source = -> [Box012]
  Type = 0
  X = 0
  Y = 0
FEATURE [TechDraw::DrawProjGroup] ProjGroup012
  Anchor = -> ProjItem011
  AutoDistribute = true
  LockPosition = false
  ProjectionType = 0
  Rotation = 0
  Scale = 0.04
  ScaleType = 0
  Source = -> [Box012]
  Views = -> [ProjItem011]
  X = 105.823
  Y = 34.0899
  spacingX = 15
  spacingY = 15
FEATURE [TechDraw::DrawViewDimension] Dimension018
  Arbitrary = false
  FormatSpec = %.2f
  LockPosition = false
  MeasureType = 1
  OverTolerance = 0
  References2D = -> [ProjItem009]
  Rotation = 0
  Scale = 0.04
  ScaleType = 0
  Type = 1
  UnderTolerance = 0
  X = -0.528907
  Y = 23.9732
FEATURE [TechDraw::DrawViewDimension] Dimension019
  Arbitrary = false
  FormatSpec = %.2f
  LockPosition = false
  MeasureType = 1
  OverTolerance = 0
  References2D = -> [ProjItem009]
  Rotation = 0
  Scale = 0.04
  ScaleType = 0
  Type = 2
  UnderTolerance = 0
  X = -33.767
  Y = 0.911909
FEATURE [TechDraw::DrawViewDimension] Dimension020
  Arbitrary = false
  FormatSpec = %.2f
  LockPosition = false
  MeasureType = 1
  OverTolerance = 0
  References2D = -> [ProjItem007]
  Rotation = 0
  Scale = 0.04
  ScaleType = 0
  Type = 1
  UnderTolerance = 0
  X = 0.911909
  Y = 27.3471
FEATURE [TechDraw::DrawViewDimension] Dimension021
  Arbitrary = false
  FormatSpec = %.2f
  LockPosition = false
  MeasureType = 1
  OverTolerance = 0
  References2D = -> [ProjItem007]
  Rotation = 0
  Scale = 0.04
  ScaleType = 0
  Type = 2
  UnderTolerance = 0
  X = -23.8911
  Y = -0.911909
FEATURE [TechDraw::DrawViewDimension] Dimension022
  Arbitrary = false
  FormatSpec = %.2f
  LockPosition = false
  MeasureType = 1
  OverTolerance = 0
  References2D = -> [ProjItem006]
  Rotation = 0
  Scale = 0.04
  ScaleType = 0
  Type = 1
  UnderTolerance = 0
  X = 0
  Y = 25.6192
FEATURE [TechDraw::DrawViewDimension] Dimension023
  Arbitrary = false
  FormatSpec = %.2f
  LockPosition = false
  MeasureType = 1
  OverTolerance = 0
  References2D = -> [ProjItem006]
  Rotation = 0
  Scale = 0.04
  ScaleType = 0
  Type = 2
  UnderTolerance = 0
  X = -32.855
  Y = -0.455955
FEATURE [TechDraw::DrawViewDimension] Dimension024
  Arbitrary = false
  FormatSpec = %.2f
  LockPosition = false
  MeasureType = 1
  OverTolerance = 0
  References2D = -> [ProjItem008]
  Rotation = 0
  Scale = 0.04
  ScaleType = 0
  Type = 2
  UnderTolerance = 0
  X = -24.3471
  Y = -0.683932
FEATURE [TechDraw::DrawViewDimension] Dimension025
  Arbitrary = false
  FormatSpec = %.2f
  LockPosition = false
  MeasureType = 1
  OverTolerance = 0
  References2D = -> [ProjItem008]
  Rotation = 0
  Scale = 0.04
  ScaleType = 0
  Type = 1
  UnderTolerance = 0
  X = 0.227977
  Y = 27.575
FEATURE [TechDraw::DrawViewDimension] Dimension026
  Arbitrary = false
  FormatSpec = %.2f
  LockPosition = false
  MeasureType = 1
  OverTolerance = 0
  References2D = -> [ProjItem010]
  Rotation = 0
  Scale = 0.04
  ScaleType = 0
  Type = 1
  UnderTolerance = 0
  X = 0.227977
  Y = 19.5233
FEATURE [TechDraw::DrawViewDimension] Dimension027
  Arbitrary = false
  FormatSpec = %.2f
  LockPosition = false
  MeasureType = 1
  OverTolerance = 0
  References2D = -> [ProjItem010]
  Rotation = 0
  Scale = 0.04
  ScaleType = 0
  Type = 2
  UnderTolerance = 0
  X = -33.083
  Y = 0
FEATURE [TechDraw::DrawViewDimension] Dimension028
  Arbitrary = false
  FormatSpec = %.2f
  LockPosition = false
  MeasureType = 1
  OverTolerance = 0
  References2D = -> [ProjItem011]
  Rotation = 0
  Scale = 0.04
  ScaleType = 0
  Type = 1
  UnderTolerance = 0
  X = 1.13989
  Y = 19.5233
FEATURE [TechDraw::DrawViewDimension] Dimension029
  Arbitrary = false
  FormatSpec = %.2f
  LockPosition = false
  MeasureType = 1
  OverTolerance = 0
  References2D = -> [ProjItem011]
  Rotation = 0
  Scale = 0.04
  ScaleType = 0
  Type = 2
  UnderTolerance = 0
  X = -33.083
  Y = 0
FEATURE [TechDraw::DrawPage] Page001  label="Shelf001"
  KeepUpdated = true
  ProjectionType = 0
  Scale = 0.04
  Template = -> Template001
  Views = -> [ProjGroup007,ProjGroup008,ProjGroup009,ProjGroup010,ProjGroup011,ProjGroup012,Dimension018,Dimension019,Dimension020,Dimension021,Dimension022,Dimension023,Dimension024,Dimension025,Dimension026,Dimension027,Dimension028,Dimension029]
FEATURE [TechDraw::DrawSVGTemplate] Template002
  EditableTexts = Designed_by_Name=Intech Studio; Drawing_number=Drawing number; FC-Date=2020.10.09.; FC-SC=0.04; FC-SH=Sheet; FC-Title=120cm ablak; Weight=Weight
  Height = 210
  Orientation = 1
  Width = 297
FEATURE [TechDraw::DrawProjGroupItem] ProjItem012  label="Front013"
  CoarseView = false
  Direction = (0,1,0)
  Focus = 100
  HardHidden = false
  IsoCount = 0
  IsoHidden = false
  IsoVisible = false
  LockPosition = true
  Perspective = false
  Rotation = 0
  RotationVector = (-1,0,0)
  Scale = 0.04
  ScaleType = 2
  SeamHidden = false
  SeamVisible = false
  SmoothHidden = false
  SmoothVisible = false
  Source = -> [Body001]
  Type = 0
  X = 0
  Y = 0
FEATURE [TechDraw::DrawProjGroup] ProjGroup013
  Anchor = -> ProjItem012
  AutoDistribute = true
  LockPosition = false
  ProjectionType = 0
  Rotation = 0
  Scale = 0.04
  ScaleType = 0
  Source = -> [Body001]
  Views = -> [ProjItem012]
  X = 98.9286
  Y = 136.844
  spacingX = 15
  spacingY = 15
FEATURE [TechDraw::DrawViewDimension] Dimension030
  Arbitrary = false
  FormatSpec = %.2f
  LockPosition = false
  MeasureType = 1
  OverTolerance = 0
  References2D = -> [ProjItem012]
  Rotation = 0
  Scale = 0.04
  ScaleType = 0
  Type = 2
  UnderTolerance = 0
  X = -38.1659
  Y = 0.578094
FEATURE [TechDraw::DrawViewDimension] Dimension031
  Arbitrary = false
  FormatSpec = %.2f
  LockPosition = false
  MeasureType = 1
  OverTolerance = 0
  References2D = -> [ProjItem012]
  Rotation = 0
  Scale = 0.04
  ScaleType = 0
  Type = 1
  UnderTolerance = 0
  X = 0.867141
  Y = 31.4407
FEATURE [TechDraw::DrawViewDimension] Dimension032
  Arbitrary = false
  FormatSpec = %.2f
  LockPosition = false
  MeasureType = 1
  OverTolerance = 0
  References2D = -> [ProjItem012]
  Rotation = 0
  Scale = 0.04
  ScaleType = 0
  Type = 2
  UnderTolerance = 0
  X = 31.8186
  Y = 28.7064
FEATURE [TechDraw::DrawPage] Page002
  KeepUpdated = true
  ProjectionType = 0
  Scale = 0.04
  Template = -> Template002
  Views = -> [ProjGroup013,Dimension030,Dimension031,Dimension032]
